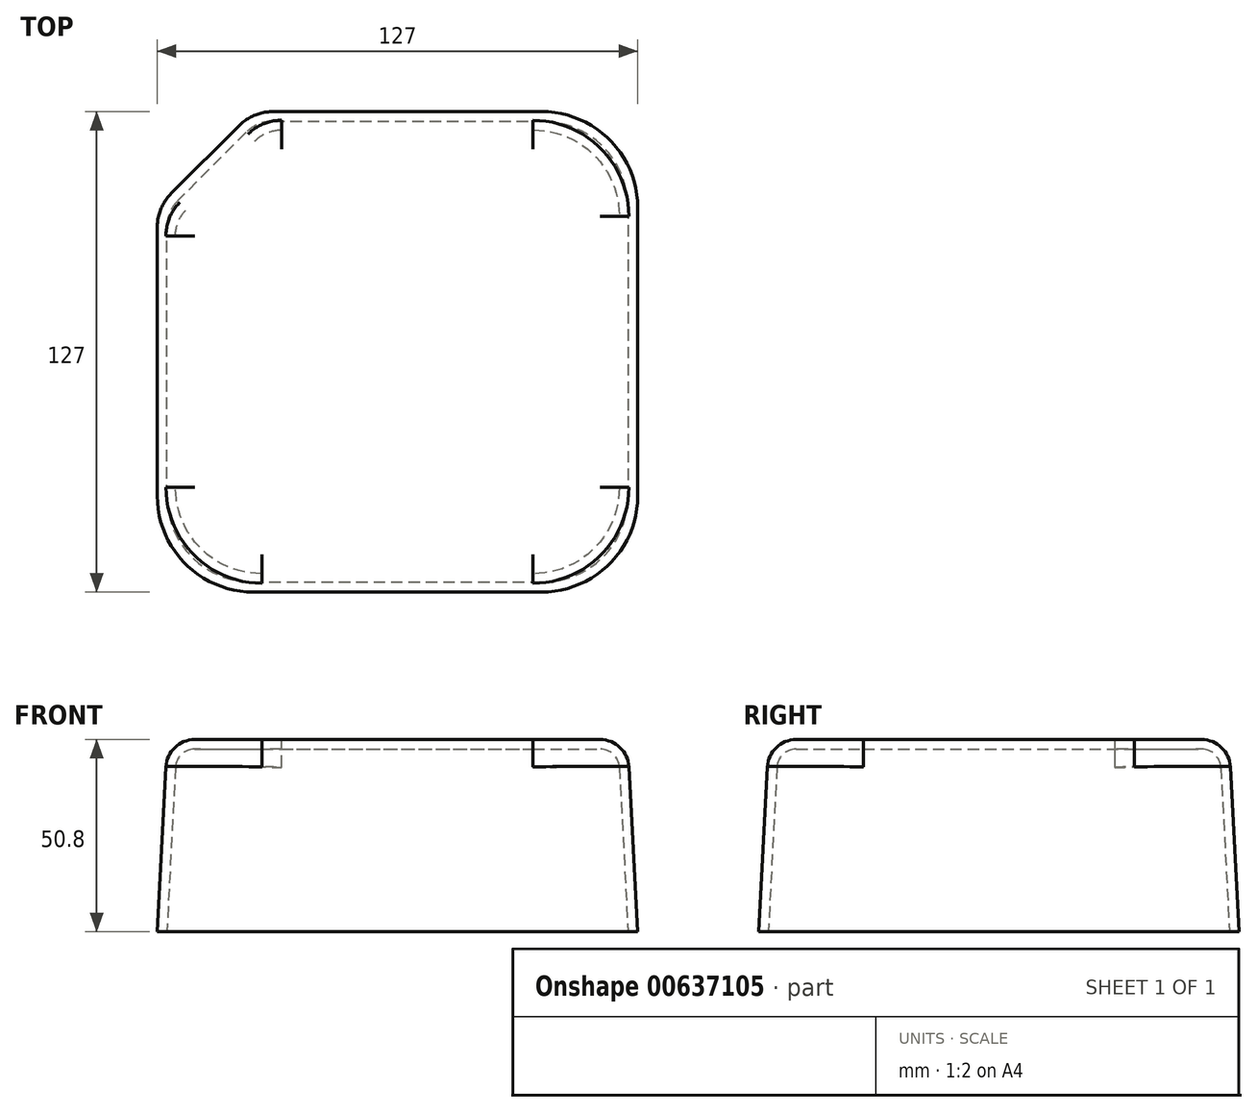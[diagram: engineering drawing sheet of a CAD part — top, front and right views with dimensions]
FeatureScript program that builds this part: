
annotation { "Feature Type Name" : "Feature", "Feature Type Description" : "" }
export const myFeature = defineFeature(function(context is Context, id is Id, definition is map)
    precondition{}
    {
        {
            var Q0;
            Q0=qCreatedBy(makeId("Top.planeOp"),FACE);
            var sketch = newSketch(context, id + "F0", { "sketchPlane" : qUnion([Q0])});
            skLineSegment(sketch, "E0.bottom", {"start": v(-63.5, 63.5) * mm, "end": v(63.5, 63.5) * mm});
            skLineSegment(sketch, "E0.top", {"start": v(-63.5, -63.5) * mm, "end": v(63.5, -63.5) * mm});
            skLineSegment(sketch, "E0.left", {"start": v(-63.5, 63.5) * mm, "end": v(-63.5, -63.5) * mm});
            skLineSegment(sketch, "E0.right", {"start": v(63.5, 63.5) * mm, "end": v(63.5, -63.5) * mm});
            skLineSegment(sketch, "E1", {"start": v(63.5, 63.5) * mm, "end": v(-63.5, -63.5) * mm, "construction": true});
            skSolve(sketch);
        }
        {
            var Q0;
            Q0 = qSketchRegion(id + "F0", true);
            extrude(context, id + "F1", {"entities" : qUnion([Q0]), "depth" : 50.8 * mm, "offsetDistance" : 25.4 * mm, "hasDraft" : true, "draftAngle" : 3 * degree, "draftPullDirection" : true});
        }
        {
            var Q0;
            Q0=makeQuery(id+"F1.opExtrude","SWEPT_EDGE",EDGE,{"disambiguationData":[OSD([sQuery(id+"F0.wireOp",EDGE,"E0.top"),sQuery(id+"F0.wireOp",EDGE,"E0.left")])]});
            var Q1;
            Q1=makeQuery(id+"F1.opExtrude","SWEPT_EDGE",EDGE,{"disambiguationData":[OSD([sQuery(id+"F0.wireOp",EDGE,"E0.top"),sQuery(id+"F0.wireOp",EDGE,"E0.right")])]});
            var Q2;
            Q2=makeQuery(id+"F1.opExtrude","SWEPT_EDGE",EDGE,{"disambiguationData":[OSD([sQuery(id+"F0.wireOp",EDGE,"E0.bottom"),sQuery(id+"F0.wireOp",EDGE,"E0.right")])]});
            fillet(context, id + "F2", {"entities" : qUnion([Q0, Q1, Q2]), "radius" : 25.4 * mm, "tangentPropagation" : true, "allowEdgeOverflow" : false});
        }
        {
            var Q0;
            Q0=makeQuery(id+"F1.opExtrude","SWEPT_EDGE",EDGE,{"disambiguationData":[OSD([sQuery(id+"F0.wireOp",EDGE,"E0.bottom"),sQuery(id+"F0.wireOp",EDGE,"E0.left")])]});
            chamfer(context, id + "F3", {"entities" : qUnion([Q0]), "width" : 25.4 * mm, "tangentPropagation" : true});
        }
        {
            var Q0;
            {var subQ0=sQuery(id+"F0.wireOp",EDGE,"E0.bottom");Q0=makeQuery(id+"F3.opChamfer","BLEND_EDGE",EDGE,{"blendedFrom":[makeQuery(id+"F1.opExtrude","SWEPT_EDGE",EDGE,{"disambiguationData":[OSD([subQ0,sQuery(id+"F0.wireOp",EDGE,"E0.left")])]}),makeQuery(id+"F1.opExtrude","SWEPT_FACE",FACE,{"disambiguationData":[OSD([subQ0])]})],"blendedInto":[makeQuery(id+"F1.opExtrude","SWEPT_FACE",FACE,{"disambiguationData":[OSD([subQ0])]})]});}
            var Q1;
            {var subQ0=sQuery(id+"F0.wireOp",EDGE,"E0.left");Q1=makeQuery(id+"F3.opChamfer","BLEND_EDGE",EDGE,{"blendedFrom":[makeQuery(id+"F1.opExtrude","SWEPT_EDGE",EDGE,{"disambiguationData":[OSD([sQuery(id+"F0.wireOp",EDGE,"E0.bottom"),subQ0])]}),makeQuery(id+"F1.opExtrude","SWEPT_FACE",FACE,{"disambiguationData":[OSD([subQ0])]})],"blendedInto":[makeQuery(id+"F1.opExtrude","SWEPT_FACE",FACE,{"disambiguationData":[OSD([subQ0])]})]});}
            fillet(context, id + "F4", {"entities" : qUnion([Q0, Q1]), "radius" : 12.7 * mm, "tangentPropagation" : true, "allowEdgeOverflow" : false});
        }
        {
            var Q0;
            Q0=makeQuery(id+"F1.opExtrude","CAP_FACE",FACE,{"disambiguationData":[OSD([sQuery(id+"F0.wireOp",EDGE,"E0.bottom"),sQuery(id+"F0.wireOp",EDGE,"E0.top"),sQuery(id+"F0.wireOp",EDGE,"E0.left"),sQuery(id+"F0.wireOp",EDGE,"E0.right")])],"isStart":false});
            fillet(context, id + "F5", {"entities" : qUnion([Q0]), "radius" : 7.62 * mm, "tangentPropagation" : true, "allowEdgeOverflow" : false});
        }
        {
            var Q0;
            Q0=makeQuery(id+"F1.opExtrude","CAP_FACE",FACE,{"disambiguationData":[OSD([sQuery(id+"F0.wireOp",EDGE,"E0.bottom"),sQuery(id+"F0.wireOp",EDGE,"E0.top"),sQuery(id+"F0.wireOp",EDGE,"E0.left"),sQuery(id+"F0.wireOp",EDGE,"E0.right")])],"isStart":true});
            shell(context, id + "F6", {"entities" : qUnion([Q0]), "thickness" : 2.54 * mm});
        }
    });
